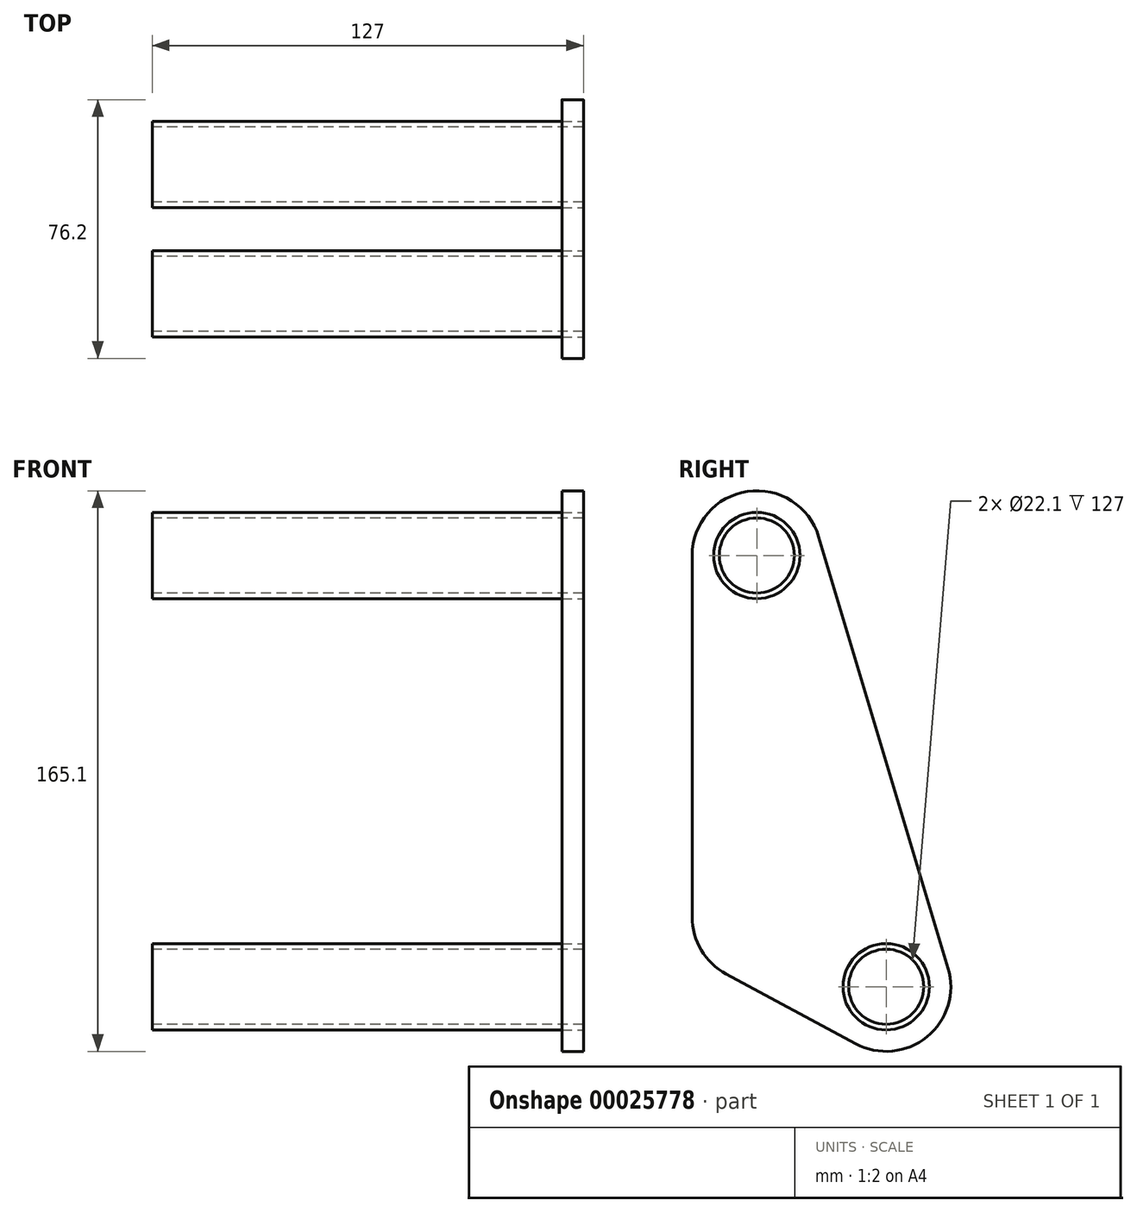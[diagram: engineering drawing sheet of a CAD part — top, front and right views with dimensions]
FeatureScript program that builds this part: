
annotation { "Feature Type Name" : "Feature", "Feature Type Description" : "" }
export const myFeature = defineFeature(function(context is Context, id is Id, definition is map)
    precondition{}
    {
        {
            var Q0;
            Q0=qCreatedBy(makeId("Right.planeOp"),FACE);
            var sketch = newSketch(context, id + "F0", { "sketchPlane" : qUnion([Q0])});
            skCircle(sketch, "E0", {"center": v(0, 0) * mm, "radius": 12.7 * mm});
            skCircle(sketch, "E1", {"center": v(-38.1, 127) * mm, "radius": 12.7 * mm});
            skLineSegment(sketch, "E2", {"start": v(-38.1, 127) * mm, "end": v(0, 0) * mm, "construction": true});
            skCircle(sketch, "E3.0", {"center": v(-38.1, 127) * mm, "radius": 11.05 * mm});
            skCircle(sketch, "E4.0", {"center": v(0, 0) * mm, "radius": 11.05 * mm});
            skSolve(sketch);
        }
        {
            var Q0;
            Q0 = qSketchRegion(id + "F0", true);
            extrude(context, id + "F1", {"entities" : qUnion([Q0]), "endBound" : BoundingType.SYMMETRIC, "depth" : 127 * mm});
        }
        {
            var Q0;
            Q0=makeQuery(id+"F1.opExtrude","CAP_FACE",FACE,{"disambiguationData":[OSD([sQuery(id+"F0.wireOp",EDGE,"E1"),sQuery(id+"F0.wireOp",EDGE,"E3.0")])],"isStart":false});
            var sketch = newSketch(context, id + "F2", { "sketchPlane" : qUnion([Q0])});
            skLineSegment(sketch, "E5", {"start": v(-57.15, 127) * mm, "end": v(-57.15, 20.52) * mm});
            skLineSegment(sketch, "E6", {"start": v(-47.13, 3.74) * mm, "end": v(-9.03, -16.77) * mm});
            skLineSegment(sketch, "E7", {"start": v(-19.85, 132.47) * mm, "end": v(18.25, 5.47) * mm});
            skArc(sketch, "E8.filletArc", {"start": v(-9.03, -16.77) * mm, "mid": v(12.04, -14.76) * mm, "end": v(18.25, 5.47) * mm});
            skArc(sketch, "E9.filletArc", {"start": v(-19.85, 132.47) * mm, "mid": v(-40.87, 145.85) * mm, "end": v(-57.15, 127) * mm});
            skPoint(sketch, "E10.visualSharp", {"position": v(-57.15, 9.14) * mm});
            skArc(sketch, "E10.filletArc", {"start": v(-57.15, 20.52) * mm, "mid": v(-54.45, 10.75) * mm, "end": v(-47.13, 3.74) * mm});
            skCircle(sketch, "E11.0", {"center": v(-38.1, 127) * mm, "radius": 12.7 * mm});
            skCircle(sketch, "E11.1", {"center": v(0, 0) * mm, "radius": 12.7 * mm});
            skSolve(sketch);
        }
        {
            var Q0;
            Q0 = qSketchRegion(id + "F2", true);
            extrude(context, id + "F3", {"entities" : qUnion([Q0]), "oppositeDirection" : true, "depth" : 6.35 * mm});
        }
    });
